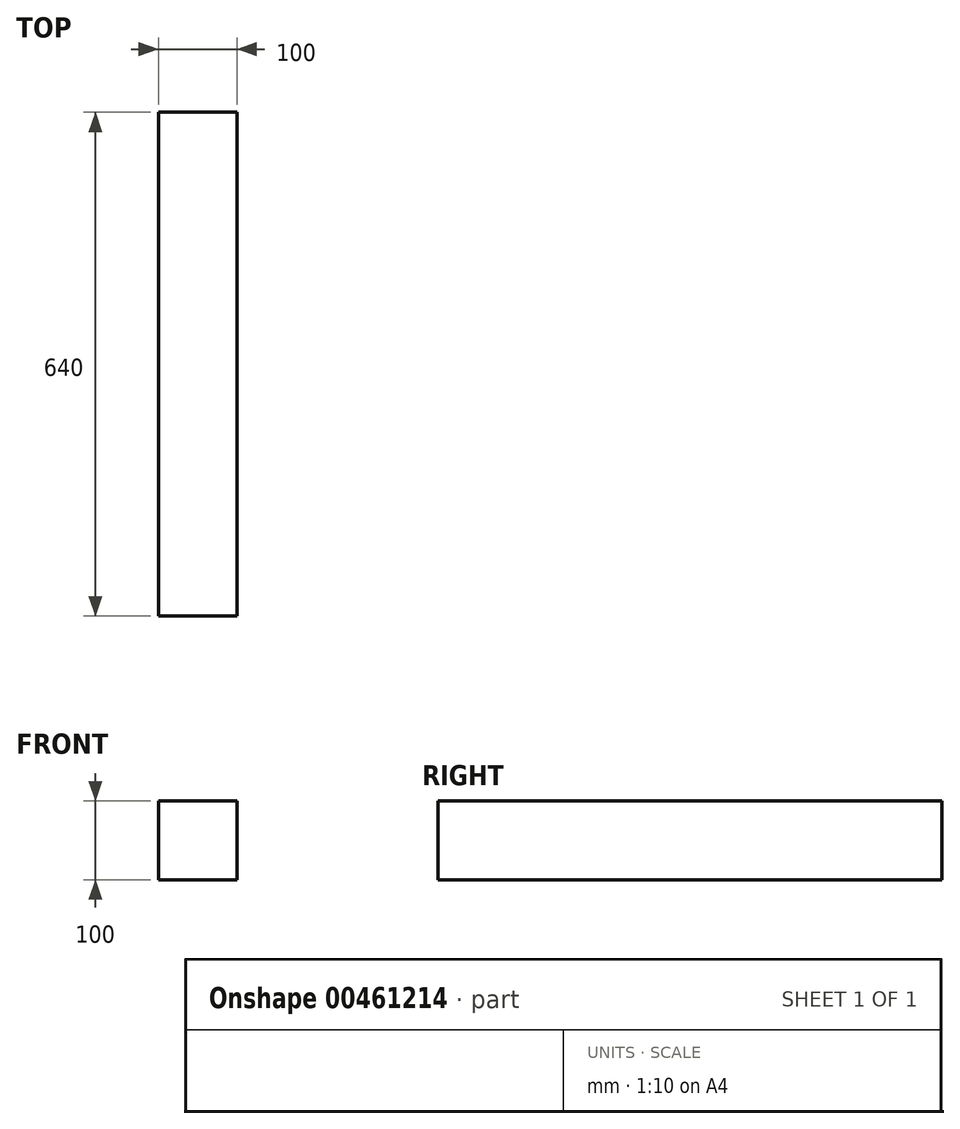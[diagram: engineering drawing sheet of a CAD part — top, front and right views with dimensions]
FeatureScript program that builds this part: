
annotation { "Feature Type Name" : "Feature", "Feature Type Description" : "" }
export const myFeature = defineFeature(function(context is Context, id is Id, definition is map)
    precondition{}
    {
        {
            var Q0;
            Q0=qCreatedBy(makeId("Front.planeOp"),FACE);
            var sketch = newSketch(context, id + "F0", { "sketchPlane" : qUnion([Q0])});
            skLineSegment(sketch, "E0.bottom", {"start": v(0, 0) * mm, "end": v(100, 0) * mm});
            skLineSegment(sketch, "E0.top", {"start": v(0, 100) * mm, "end": v(100, 100) * mm});
            skLineSegment(sketch, "E0.left", {"start": v(0, 0) * mm, "end": v(0, 100) * mm});
            skLineSegment(sketch, "E0.right", {"start": v(100, 0) * mm, "end": v(100, 100) * mm});
            skSolve(sketch);
        }
        {
            var Q0;
            Q0 = qSketchRegion(id + "F0", true);
            extrude(context, id + "F1", {"entities" : qUnion([Q0]), "depth" : 640 * mm});
        }
    });
